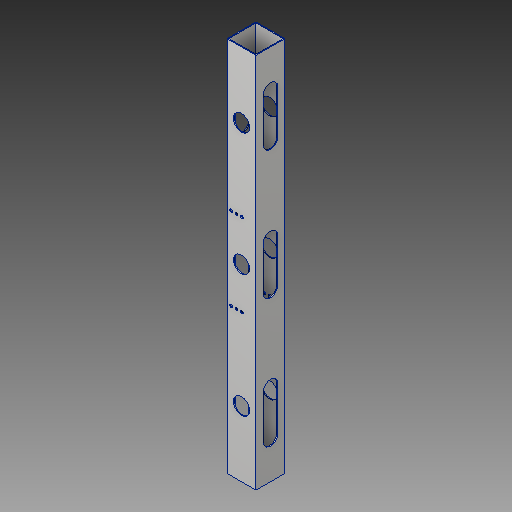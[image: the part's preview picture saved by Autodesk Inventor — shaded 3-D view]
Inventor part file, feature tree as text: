
AUTODESK INVENTOR PART (.ipt)
format: ipt  version: 2018 (Build 220112000, 112)  size: 217,088 bytes
history: native  units: in
note: dims shown in document units (in); Inventor stores cm internally (conversion verified against a paired STEP export)
features: extrude x6, sketch x6
ambient origin geometry x8: Origin, YZ Plane, XZ Plane, XY Plane, X Axis, Y Axis, Z Axis, Center Point
bodies: Solid1 (feature_tree)
feature tree (12):
  extrude  "Extrusion1"  Depth=2.0in
  extrude  "Extrusion2"  Depth=0.0625in
  extrude  "Extrusion3"  Depth=0.0625in
  extrude  "Extrusion4"  Depth=26.0in
  extrude  "Extrusion5"  Depth=20.875in TaperAngle=0.0deg
  extrude  "Extrusion6"  Depth=1.0in
  sketch  "Sketch1"  dims[d0=2.0in d1=2.0in]
  sketch  "Sketch2"  dims[d2=0.0625in d3=0.0625in]
  sketch  "Sketch3"  dims[d4=0.0625in d5=0.0625in]
  sketch  "Sketch4"  dims[d6=26.0in d7=0.0in d8=4.125in]
  sketch  "Sketch5"  dims[d9=4.125in d11=20.875in d12=0.0in]
  sketch  "Sketch6"  dims[d15=0.2in d16=0.375in d17=0.375in d18=4.0in d19=0.0in d20=1.0in d21=1.0in d22=2.625in d25=1.0in d27=1.0in d28=3.0in d29=5.0in d30=0.0in d31=1.0in d32=1.0in d33=2.625in d34=1.0in d35=1.0in d36=3.0in d37=5.0in d38=0.0in d39=1.0in d40=1.0in d41=1.0in d42=1.0in d43=11.5in d44=3.0in d45=5.0in d46=0.0in d47=8.4646in d48=8.4646in d49=0.978in d50=0.375in d51=0.375in d52=2.844in d53=0.978in d54=2.844in]
